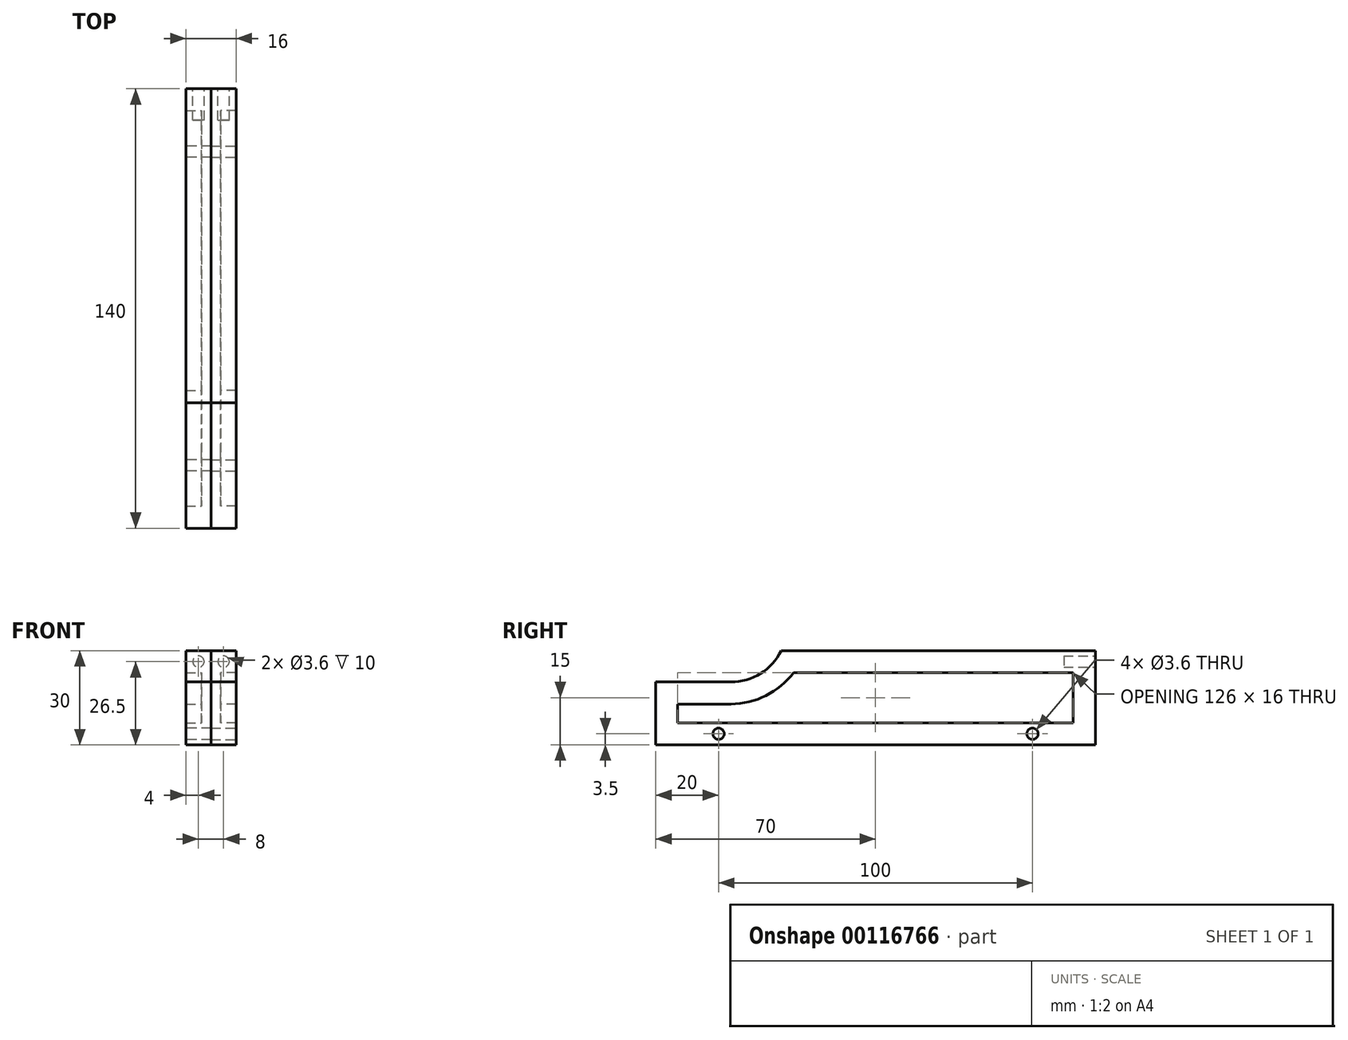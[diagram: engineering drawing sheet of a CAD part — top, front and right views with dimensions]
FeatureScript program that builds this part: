
annotation { "Feature Type Name" : "Feature", "Feature Type Description" : "" }
export const myFeature = defineFeature(function(context is Context, id is Id, definition is map)
    precondition{}
    {
        {
            var Q0;
            Q0=qCreatedBy(makeId("Right.planeOp"),FACE);
            var sketch = newSketch(context, id + "F0", { "sketchPlane" : qUnion([Q0])});
            skLineSegment(sketch, "E0", {"start": v(0, 0) * mm, "end": v(-140, 0) * mm});
            skLineSegment(sketch, "E1", {"start": v(-140, 0) * mm, "end": v(-140, 20) * mm});
            skLineSegment(sketch, "E2", {"start": v(-140, 20) * mm, "end": v(-116.09, 20) * mm});
            skLineSegment(sketch, "E3", {"start": v(-100, 30) * mm, "end": v(0, 30) * mm});
            skLineSegment(sketch, "E4", {"start": v(0, 30) * mm, "end": v(0, 0) * mm});
            skArc(sketch, "E5", {"start": v(-116.09, 20) * mm, "mid": v(-106.62, 22.7) * mm, "end": v(-100, 30) * mm});
            skSolve(sketch);
        }
        {
            var Q0;
            Q0=makeQuery(id+"F0.imprint","IMPRINT",FACE,{"disambiguationData":[TD([[makeQuery(id+"F0.imprint","IMPRINT",EDGE,{"derivedFrom":sQuery(id+"F0.wireOp",EDGE,"E0")}),-1.0]])]});
            extrude(context, id + "F1", {"entities" : qUnion([Q0]), "depth" : 3 * mm});
        }
        {
            var Q0;
            Q0=makeQuery(id+"F1.opExtrude","CAP_FACE",FACE,{"disambiguationData":[OSD([sQuery(id+"F0.wireOp",EDGE,"E0"),sQuery(id+"F0.wireOp",EDGE,"E1"),sQuery(id+"F0.wireOp",EDGE,"E2"),sQuery(id+"F0.wireOp",EDGE,"E3"),sQuery(id+"F0.wireOp",EDGE,"E4"),sQuery(id+"F0.wireOp",EDGE,"E5")])],"isStart":false});
            var sketch = newSketch(context, id + "F2", { "sketchPlane" : qUnion([Q0])});
            skLineSegment(sketch, "E6.0", {"start": v(-133, 7) * mm, "end": v(-133, 13) * mm});
            skArc(sketch, "E6.1", {"start": v(-116.09, 13) * mm, "mid": v(-104.92, 15.64) * mm, "end": v(-96.12, 23) * mm});
            skLineSegment(sketch, "E6.2", {"start": v(-96.12, 23) * mm, "end": v(-7, 23) * mm});
            skLineSegment(sketch, "E6.3", {"start": v(-133, 13) * mm, "end": v(-116.09, 13) * mm});
            skLineSegment(sketch, "E6.4", {"start": v(-7, 23) * mm, "end": v(-7, 7) * mm});
            skLineSegment(sketch, "E6.5", {"start": v(-7, 7) * mm, "end": v(-133, 7) * mm});
            skSolve(sketch);
        }
        {
            var Q0;
            {var subQ5=sQuery(id+"F2.wireOp",EDGE,"E6.0");Q0=makeQuery(id+"F2.imprint","IMPRINT",FACE,{"disambiguationData":[TD([[makeQuery(id+"F2.imprint","IMPRINT",EDGE,{"derivedFrom":subQ5}),1.0]])]});}
            extrude(context, id + "F3", {"entities" : qUnion([Q0]), "operationType" : NewBodyOperationType.ADD, "depth" : 5 * mm});
        }
        {
            var Q0;
            Q0=makeQuery(id+"F3.opExtrude","CAP_FACE",FACE,{"disambiguationData":[OSD([sQuery(id+"F0.wireOp",EDGE,"E0"),sQuery(id+"F0.wireOp",EDGE,"E1"),sQuery(id+"F0.wireOp",EDGE,"E2"),sQuery(id+"F0.wireOp",EDGE,"E3"),sQuery(id+"F0.wireOp",EDGE,"E4"),sQuery(id+"F0.wireOp",EDGE,"E5"),sQuery(id+"F2.wireOp",EDGE,"E6.0"),sQuery(id+"F2.wireOp",EDGE,"E6.1"),sQuery(id+"F2.wireOp",EDGE,"E6.2"),sQuery(id+"F2.wireOp",EDGE,"E6.3"),sQuery(id+"F2.wireOp",EDGE,"E6.4"),sQuery(id+"F2.wireOp",EDGE,"E6.5")])],"isStart":false});
            var sketch = newSketch(context, id + "F4", { "sketchPlane" : qUnion([Q0])});
            skLineSegment(sketch, "E7", {"start": v(0, 0) * mm, "end": v(-20, 0) * mm, "construction": true});
            skLineSegment(sketch, "E8", {"start": v(-20, 0) * mm, "end": v(-20, 3.5) * mm, "construction": true});
            skCircle(sketch, "E9", {"center": v(-20, 3.5) * mm, "radius": 1.8 * mm});
            skLineSegment(sketch, "E10", {"start": v(-20, 3.5) * mm, "end": v(-120, 3.5) * mm, "construction": true});
            skCircle(sketch, "E11", {"center": v(-120, 3.5) * mm, "radius": 1.8 * mm});
            skSolve(sketch);
        }
        {
            var Q0;
            Q0 = qSketchRegion(id + "F4", true);
            extrude(context, id + "F5", {"entities" : qUnion([Q0]), "operationType" : NewBodyOperationType.REMOVE, "endBound" : BoundingType.THROUGH_ALL, "oppositeDirection" : true, "depth" : 25 * mm});
        }
        {
            var Q0;
            {var subQ0=sQuery(id+"F0.wireOp",EDGE,"E4");Q0=makeQuery(id+"F3.boolean.opBoolean","MERGE",FACE,{"derivedFrom":[makeQuery(id+"F1.opExtrude","SWEPT_FACE",FACE,{"disambiguationData":[OSD([subQ0])]}),makeQuery(id+"F3.opExtrude","SWEPT_FACE",FACE,{"disambiguationData":[OSD([subQ0])]})]});}
            var sketch = newSketch(context, id + "F6", { "sketchPlane" : qUnion([Q0])});
            skLineSegment(sketch, "E12", {"start": v(-8, 30) * mm, "end": v(-4, 30) * mm, "construction": true});
            skLineSegment(sketch, "E13", {"start": v(-4, 30) * mm, "end": v(-4, 26.5) * mm, "construction": true});
            skCircle(sketch, "E14", {"center": v(-4, 26.5) * mm, "radius": 1.8 * mm});
            skSolve(sketch);
        }
        {
            var Q0;
            Q0 = qSketchRegion(id + "F6", true);
            extrude(context, id + "F7", {"entities" : qUnion([Q0]), "operationType" : NewBodyOperationType.REMOVE, "oppositeDirection" : true, "depth" : 10 * mm});
        }
        {
            var Q0;
            Q0=makeQuery(id+"F1.opExtrude","SWEPT_BODY",BODY,{"disambiguationData":[OSD([sQuery(id+"F0.wireOp",EDGE,"E0"),sQuery(id+"F0.wireOp",EDGE,"E1"),sQuery(id+"F0.wireOp",EDGE,"E2"),sQuery(id+"F0.wireOp",EDGE,"E3"),sQuery(id+"F0.wireOp",EDGE,"E4"),sQuery(id+"F0.wireOp",EDGE,"E5")])]});
            var Q1;
            Q1=qCreatedBy(makeId("Right.planeOp"),FACE);
            mirror(context, id + "F8", {"entities" : qUnion([Q0]), "mirrorPlane" : qUnion([Q1])});
        }
    });
